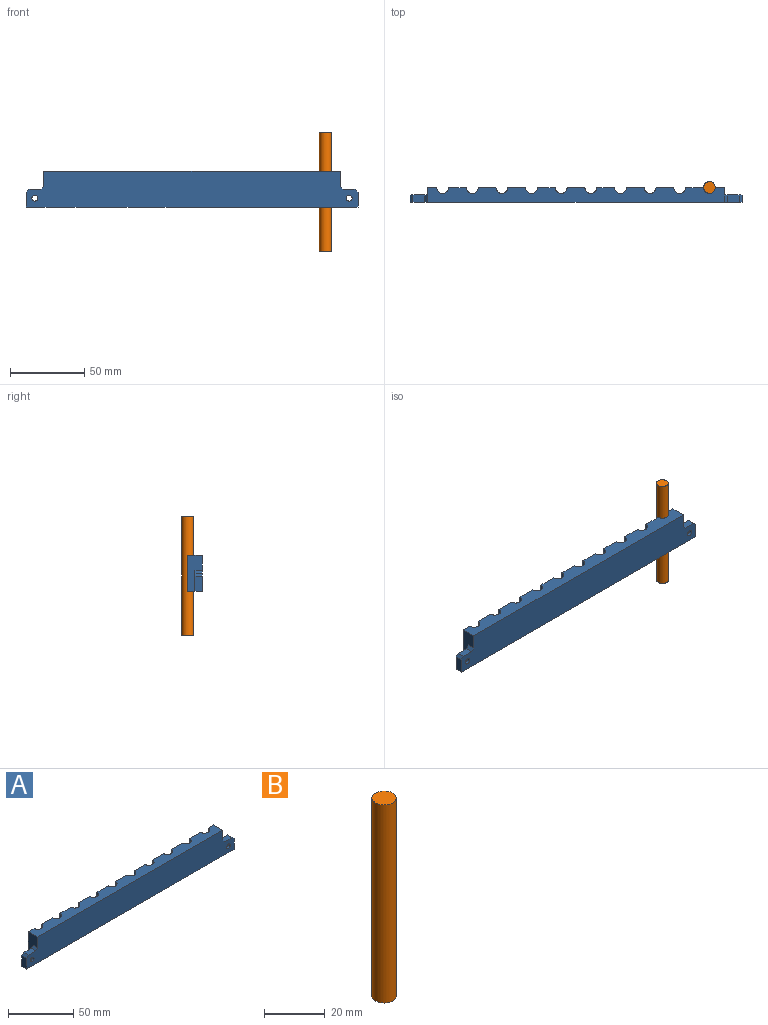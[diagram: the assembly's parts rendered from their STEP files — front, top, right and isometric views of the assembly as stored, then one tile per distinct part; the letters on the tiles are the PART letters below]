
ASSEMBLY  parts=2 mates=1
PART A: 80 faces, bbox 224x10x24 mm
  f0: plane 24x10mm, normal (-1,0,0), area 170mm2, adj f4,f5,f6,f9,f69,f75
  f1: plane 18x9mm, normal (0,0,-1), area 70.7mm2, adj f2,f4,f7,f8
  f2: plane 24x12mm, normal (0,1,0), area 168mm2, adj f1,f3,f6,f7,f8,f9,f10,f61
  f3: cylinder r=4mm len=24mm, axis (0,0,-1), area 301.6mm2, adj f2,f4,f6,f9
  f4: plane 24x6mm, normal (0,1,0), area 84mm2, adj f0,f1,f3,f6,f7,f8,f9,f10
  f5: plane 224x24mm, normal (0,-1,0), area 5062.9mm2, adj f0,f6,f9,f52,f66,f67,f68,f70
  f6: plane 200x10mm, normal (0,0,1), area 1748.7mm2, adj f0,f2,f3,f4,f5,f12,f13,f14
  f7: cylinder r=9mm len=20mm, axis (0,0,-1), area 565.5mm2, adj f1,f2,f4,f10
  f8: cylinder r=6mm len=20mm, axis (0,0,-1), area 377mm2, adj f1,f2,f4,f10
  f9: plane 224x10mm, normal (0,0,-1), area 1868.7mm2, adj f0,f2,f3,f4,f5,f12,f13,f14
  f10: plane 18x9mm, normal (0,0,1), area 70.7mm2, adj f2,f4,f7,f8
  f11: plane 18x9mm, normal (0,0,-1), area 70.7mm2, adj f12,f14,f15,f16
  f12: plane 24x12mm, normal (0,1,0), area 168mm2, adj f6,f9,f11,f13,f15,f16,f17,f18
  f13: cylinder r=4mm len=24mm, axis (0,0,-1), area 301.6mm2, adj f6,f9,f12,f14
  f14: plane 24x12mm, normal (0,1,0), area 168mm2, adj f6,f9,f11,f13,f15,f16,f17,f61
  f15: cylinder r=9mm len=20mm, axis (0,0,-1), area 565.5mm2, adj f11,f12,f14,f17
  f16: cylinder r=6mm len=20mm, axis (0,0,-1), area 377mm2, adj f11,f12,f14,f17
  f17: plane 18x9mm, normal (0,0,1), area 70.7mm2, adj f12,f14,f15,f16
  f18: plane 18x9mm, normal (0,0,-1), area 70.7mm2, adj f12,f19,f21,f22
  f19: plane 24x12mm, normal (0,1,0), area 168mm2, adj f6,f9,f18,f20,f21,f22,f23,f24
  f20: cylinder r=4mm len=24mm, axis (0,0,-1), area 301.6mm2, adj f6,f9,f12,f19
  f21: cylinder r=9mm len=20mm, axis (0,0,-1), area 565.5mm2, adj f12,f18,f19,f23
  f22: cylinder r=6mm len=20mm, axis (0,0,-1), area 377mm2, adj f12,f18,f19,f23
  f23: plane 18x9mm, normal (0,0,1), area 70.7mm2, adj f12,f19,f21,f22
  f24: plane 18x9mm, normal (0,0,-1), area 70.7mm2, adj f19,f25,f27,f28
  f25: plane 24x12mm, normal (0,1,0), area 168mm2, adj f6,f9,f24,f26,f27,f28,f29,f30
  f26: cylinder r=4mm len=24mm, axis (0,0,-1), area 301.6mm2, adj f6,f9,f19,f25
  f27: cylinder r=9mm len=20mm, axis (0,0,-1), area 565.5mm2, adj f19,f24,f25,f29
  f28: cylinder r=6mm len=20mm, axis (0,0,-1), area 377mm2, adj f19,f24,f25,f29
  f29: plane 18x9mm, normal (0,0,1), area 70.7mm2, adj f19,f25,f27,f28
  f30: plane 18x9mm, normal (0,0,-1), area 70.7mm2, adj f25,f31,f33,f34
  f31: plane 24x12mm, normal (0,1,0), area 168mm2, adj f6,f9,f30,f32,f33,f34,f35,f36
  f32: cylinder r=4mm len=24mm, axis (0,0,-1), area 301.6mm2, adj f6,f9,f25,f31
  f33: cylinder r=9mm len=20mm, axis (0,0,-1), area 565.5mm2, adj f25,f30,f31,f35
  f34: cylinder r=6mm len=20mm, axis (0,0,-1), area 377mm2, adj f25,f30,f31,f35
  f35: plane 18x9mm, normal (0,0,1), area 70.7mm2, adj f25,f31,f33,f34
  f36: plane 18x9mm, normal (0,0,-1), area 70.7mm2, adj f31,f37,f39,f40
  f37: plane 24x12mm, normal (0,1,0), area 168mm2, adj f6,f9,f36,f38,f39,f40,f41,f42
  f38: cylinder r=4mm len=24mm, axis (0,0,-1), area 301.6mm2, adj f6,f9,f31,f37
  f39: cylinder r=9mm len=20mm, axis (0,0,-1), area 565.5mm2, adj f31,f36,f37,f41
  f40: cylinder r=6mm len=20mm, axis (0,0,-1), area 377mm2, adj f31,f36,f37,f41
  f41: plane 18x9mm, normal (0,0,1), area 70.7mm2, adj f31,f37,f39,f40
  f42: plane 18x9mm, normal (0,0,-1), area 70.7mm2, adj f37,f43,f45,f46
  f43: plane 24x12mm, normal (0,1,0), area 168mm2, adj f6,f9,f42,f44,f45,f46,f47,f56
  f44: cylinder r=4mm len=24mm, axis (0,0,-1), area 301.6mm2, adj f6,f9,f37,f43
  f45: cylinder r=9mm len=20mm, axis (0,0,-1), area 565.5mm2, adj f37,f42,f43,f47
  f46: cylinder r=6mm len=20mm, axis (0,0,-1), area 377mm2, adj f37,f42,f43,f47
  f47: plane 18x9mm, normal (0,0,1), area 70.7mm2, adj f37,f43,f45,f46
  f48: plane 18x9mm, normal (0,0,-1), area 70.7mm2, adj f49,f51,f53,f54
  f49: plane 24x6mm, normal (0,1,0), area 84mm2, adj f6,f9,f48,f50,f52,f53,f54,f55
  f50: cylinder r=4mm len=24mm, axis (0,0,-1), area 301.6mm2, adj f6,f9,f49,f51
  f51: plane 24x12mm, normal (0,1,0), area 168mm2, adj f6,f9,f48,f50,f53,f54,f55,f56
  f52: plane 24x10mm, normal (1,0,0), area 170mm2, adj f5,f6,f9,f49,f73,f76
  f53: cylinder r=9mm len=20mm, axis (0,0,-1), area 565.5mm2, adj f48,f49,f51,f55
  f54: cylinder r=6mm len=20mm, axis (0,0,-1), area 377mm2, adj f48,f49,f51,f55
  f55: plane 18x9mm, normal (0,0,1), area 70.7mm2, adj f49,f51,f53,f54
  f56: plane 18x9mm, normal (0,0,-1), area 70.7mm2, adj f43,f51,f58,f59
  f57: cylinder r=4mm len=24mm, axis (0,0,-1), area 301.6mm2, adj f6,f9,f43,f51
  f58: cylinder r=9mm len=20mm, axis (0,0,-1), area 565.5mm2, adj f43,f51,f56,f60
  f59: cylinder r=6mm len=20mm, axis (0,0,-1), area 377mm2, adj f43,f51,f56,f60
  f60: plane 18x9mm, normal (0,0,1), area 70.7mm2, adj f43,f51,f58,f59
  f61: plane 18x9mm, normal (0,0,-1), area 70.7mm2, adj f2,f14,f63,f64
  f62: cylinder r=4mm len=24mm, axis (0,0,-1), area 301.6mm2, adj f2,f6,f9,f14
  f63: cylinder r=9mm len=20mm, axis (0,0,-1), area 565.5mm2, adj f2,f14,f61,f65
  f64: cylinder r=6mm len=20mm, axis (0,0,-1), area 377mm2, adj f2,f14,f61,f65
  f65: plane 18x9mm, normal (0,0,1), area 70.7mm2, adj f2,f14,f63,f64
  f66: plane 8x5mm, normal (0,0,1), area 40mm2, adj f5,f69,f74,f75
  f67: plane 10x5mm, normal (-1,0,0), area 50mm2, adj f5,f9,f69,f74
  f68: cylinder r=2mm len=4mm, axis (0,-1,0), area 25.1mm2, adj f5,f79
  f69: plane 14x12mm, normal (0,1,0), area 65.5mm2, adj f0,f9,f66,f67,f74,f75,f79
  f70: plane 10x5mm, normal (1,0,0), area 50mm2, adj f5,f9,f73,f77
  f71: plane 8x5mm, normal (0,0,1), area 40mm2, adj f5,f73,f76,f77
  f72: cylinder r=2mm len=4mm, axis (0,-1,0), area 25.1mm2, adj f5,f78
  f73: plane 14x12mm, normal (0,1,0), area 65.5mm2, adj f9,f52,f70,f71,f76,f77,f78
  f74: plane 5x2mm, normal (-0.71,0,0.71), area 14.1mm2, adj f5,f66,f67,f69
  f75: plane 5x2mm, normal (-0.71,0,0.71), area 14.1mm2, adj f0,f5,f66,f69
  f76: plane 5x2mm, normal (0.71,0,0.71), area 14.1mm2, adj f5,f52,f71,f73
  f77: plane 5x2mm, normal (0.71,0,0.71), area 14.1mm2, adj f5,f70,f71,f73
  f78: cone r=2mm half-angle=45deg, axis (0,1,0), area 93.3mm2, adj f72,f73
  f79: cone r=5mm half-angle=45deg, axis (0,1,0), area 93.3mm2, adj f68,f69
PART B: 3 faces, bbox 8x8x80 mm
  f0: cylinder r=4mm len=80mm, axis (0,0,-1), area 2010.6mm2, adj f1,f2
  f1: plane 8x8mm, normal (0,0,1), area 50.3mm2, adj f0
  f2: plane 8x8mm, normal (0,0,-1), area 50.3mm2, adj f0
PLACE A t=(4.36,-7.45,0)mm fixed
PLACE B t=(184.36,2.55,-41.85)mm
MATE slider B.f0 <-> A.f50  axis (0,0,1) through (184.36,2.55,-1.85)mm
